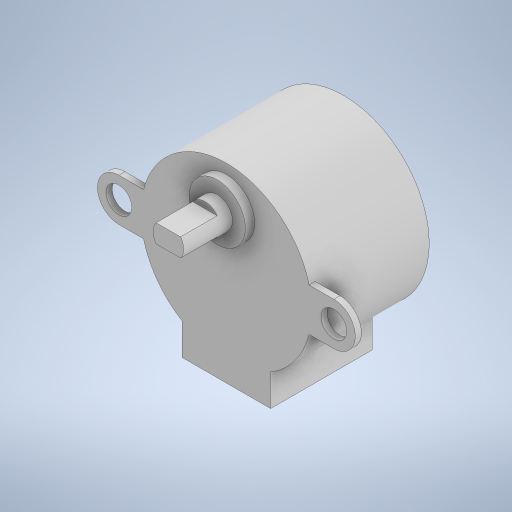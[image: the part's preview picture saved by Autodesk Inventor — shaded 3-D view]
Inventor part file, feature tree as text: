
AUTODESK INVENTOR PART (.ipt)
format: ipt  version: 2023.1 (Build 271208000, 208)  size: 297,472 bytes
history: native  units: mm
features: extrude x6, sketch x5, other x2, projected_geometry x2, mirror x1
ambient origin geometry x8: Origin, YZ Plane, XZ Plane, XY Plane, X Axis, Y Axis, Z Axis, Center Point
bodies: Body1 (feature_tree)
feature tree (16):
  other  "솔리드1"
  sketch  "스케치1"
  extrude  "돌출1"  Depth=28.0mm
  extrude  "돌출2"  Depth=5.2mm
  extrude  "돌출3"  Depth=14.5mm
  mirror  "미러1"
  extrude  "돌출4"  Depth=19.2mm TaperAngle=0.0deg
  extrude  "돌출5"  Depth=16.6mm TaperAngle=0.0deg
  extrude  "돌출6"  Depth=4.2mm
  sketch  "스케치2"
  other  "작업 평면1"
  sketch  "스케치3"
  sketch  "스케치4"
  projected_geometry  "투영된 루프1"
  sketch  "스케치5"
  projected_geometry  "투영된 루프2"
